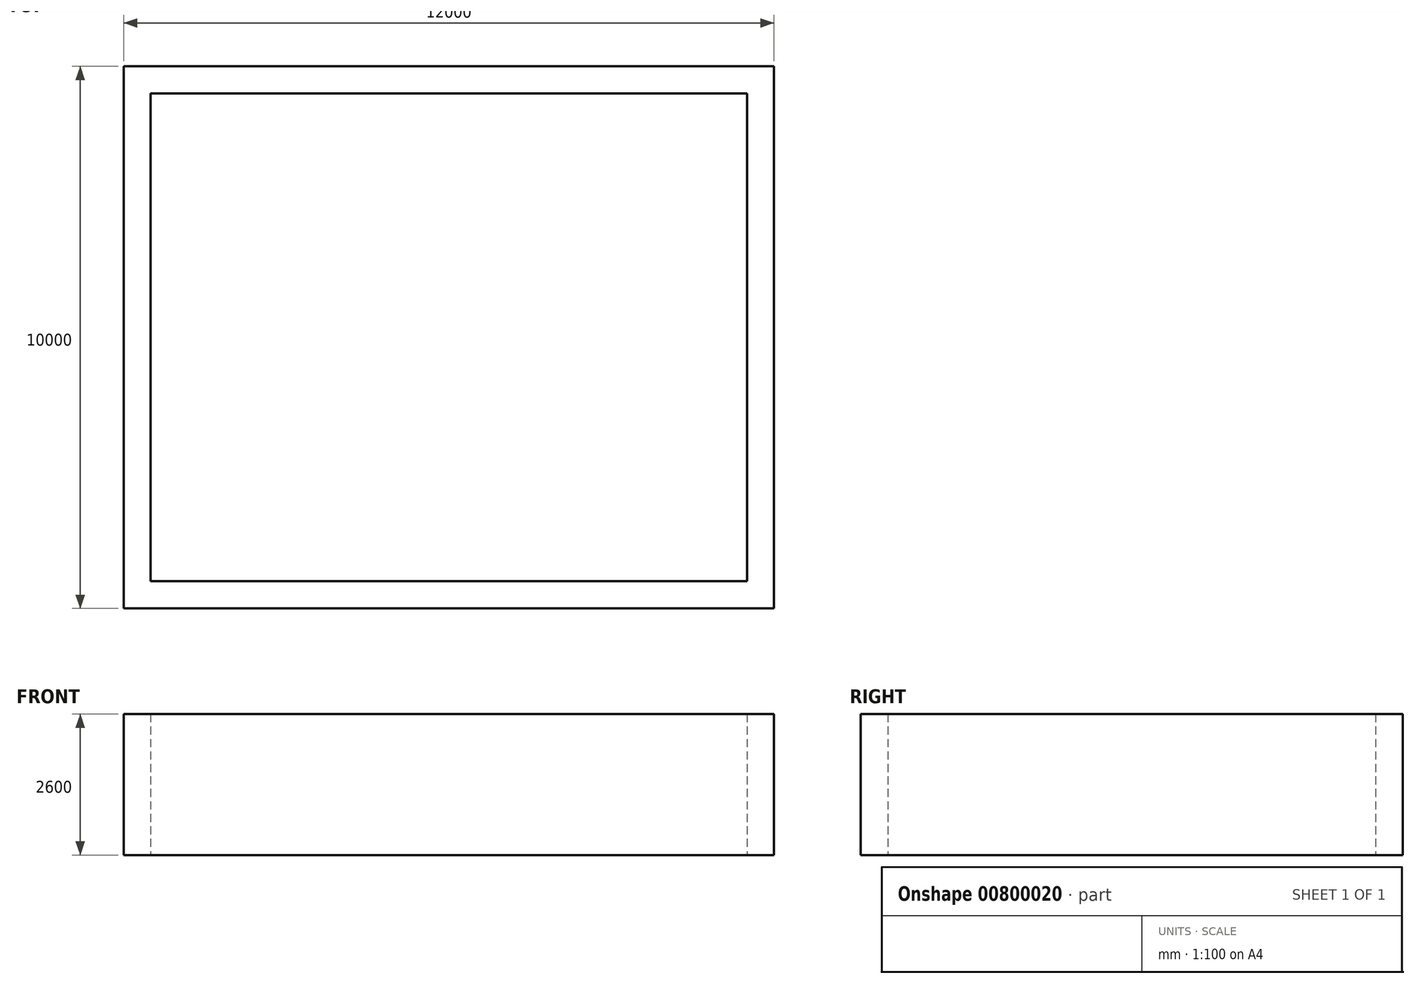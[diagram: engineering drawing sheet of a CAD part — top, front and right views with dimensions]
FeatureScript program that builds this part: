
annotation { "Feature Type Name" : "Feature", "Feature Type Description" : "" }
export const myFeature = defineFeature(function(context is Context, id is Id, definition is map)
    precondition{}
    {
        {
            var Q0;
            Q0=qCreatedBy(makeId("Top.planeOp"),FACE);
            var sketch = newSketch(context, id + "F0", { "sketchPlane" : qUnion([Q0])});
            skLineSegment(sketch, "E0.bottom", {"start": v(6000, 5000) * mm, "end": v(-6000, 5000) * mm});
            skLineSegment(sketch, "E0.top", {"start": v(6000, -5000) * mm, "end": v(-6000, -5000) * mm});
            skLineSegment(sketch, "E0.left", {"start": v(6000, 5000) * mm, "end": v(6000, -5000) * mm});
            skLineSegment(sketch, "E0.right", {"start": v(-6000, 5000) * mm, "end": v(-6000, -5000) * mm});
            skPoint(sketch, "E0.middle", {"position": v(0, 0) * mm});
            skLineSegment(sketch, "E1.0", {"start": v(-5500, 4500) * mm, "end": v(-5500, -4500) * mm});
            skLineSegment(sketch, "E1.1", {"start": v(5500, 4500) * mm, "end": v(-5500, 4500) * mm});
            skLineSegment(sketch, "E1.2", {"start": v(5500, 4500) * mm, "end": v(5500, -4500) * mm});
            skLineSegment(sketch, "E1.3", {"start": v(5500, -4500) * mm, "end": v(-5500, -4500) * mm});
            skSolve(sketch);
        }
        {
            var Q0;
            Q0=makeQuery(id+"F0.imprint","IMPRINT",FACE,{"disambiguationData":[TD([[makeQuery(id+"F0.imprint","IMPRINT",EDGE,{"derivedFrom":sQuery(id+"F0.wireOp",EDGE,"E0.bottom")}),1.0]])]});
            extrude(context, id + "F1", {"entities" : qUnion([Q0]), "depth" : 2600 * mm, "offsetDistance" : 25 * mm});
        }
    });
